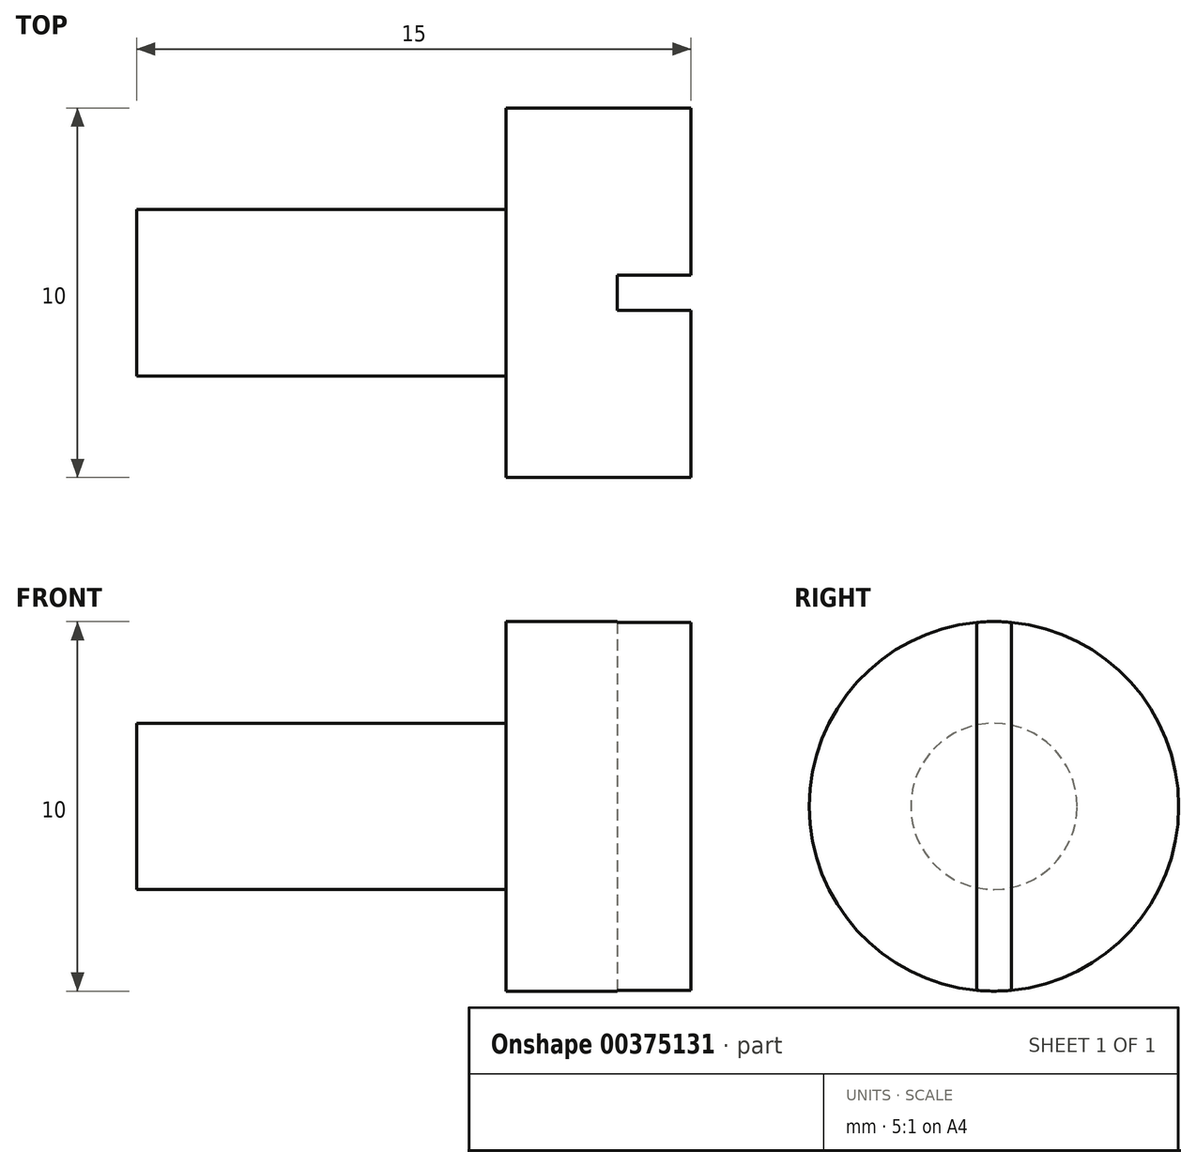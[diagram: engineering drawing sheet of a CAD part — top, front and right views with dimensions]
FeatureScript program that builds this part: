
annotation { "Feature Type Name" : "Feature", "Feature Type Description" : "" }
export const myFeature = defineFeature(function(context is Context, id is Id, definition is map)
    precondition{}
    {
        {
            var Q0;
            Q0=qCreatedBy(makeId("Right.planeOp"),FACE);
            var sketch = newSketch(context, id + "F0", { "sketchPlane" : qUnion([Q0])});
            skCircle(sketch, "E0", {"center": v(0, 0) * mm, "radius": 5 * mm});
            skSolve(sketch);
        }
        {
            var Q0;
            Q0 = qSketchRegion(id + "F0", true);
            extrude(context, id + "F1", {"entities" : qUnion([Q0]), "depth" : 5 * mm});
        }
        {
            var Q0;
            Q0=makeQuery(id+"F1.opExtrude","CAP_FACE",FACE,{"disambiguationData":[OSD([sQuery(id+"F0.wireOp",EDGE,"E0")])],"isStart":true});
            var sketch = newSketch(context, id + "F2", { "sketchPlane" : qUnion([Q0])});
            skCircle(sketch, "E1", {"center": v(0, 0) * mm, "radius": 2.25 * mm});
            skSolve(sketch);
        }
        {
            var Q0;
            Q0 = qSketchRegion(id + "F2", true);
            extrude(context, id + "F3", {"entities" : qUnion([Q0]), "operationType" : NewBodyOperationType.ADD, "depth" : 10 * mm});
        }
        {
            var Q0;
            Q0=makeQuery(id+"F1.opExtrude","CAP_FACE",FACE,{"disambiguationData":[OSD([sQuery(id+"F0.wireOp",EDGE,"E0")])],"isStart":false});
            var sketch = newSketch(context, id + "F4", { "sketchPlane" : qUnion([Q0])});
            skLineSegment(sketch, "E2.bottom", {"start": v(0.47, 6.5) * mm, "end": v(-0.47, 6.5) * mm});
            skLineSegment(sketch, "E2.top", {"start": v(0.47, -6.5) * mm, "end": v(-0.47, -6.5) * mm});
            skLineSegment(sketch, "E2.left", {"start": v(0.47, 6.5) * mm, "end": v(0.47, -6.5) * mm});
            skLineSegment(sketch, "E2.right", {"start": v(-0.47, 6.5) * mm, "end": v(-0.47, -6.5) * mm});
            skPoint(sketch, "E2.middle", {"position": v(0, 0) * mm});
            skSolve(sketch);
        }
        {
            var Q0;
            {var subQ0=sQuery(id+"F4.wireOp",EDGE,"E2.bottom");Q0=makeQuery(id+"F4.imprint","IMPRINT",FACE,{"disambiguationData":[TD([[makeQuery(id+"F4.imprint","IMPRINT",EDGE,{"derivedFrom":subQ0}),1.0]])]});}
            var Q1;
            {var subQ0=sQuery(id+"F4.wireOp",EDGE,"E2.left");var subQ1=makeQuery(id+"F1.opExtrude","CAP_EDGE",EDGE,{"disambiguationData":[OSD([sQuery(id+"F0.wireOp",EDGE,"E0")])],"isStart":false});var subQ2=makeQuery(id+"F4.imprint","INTERSECT",VERTEX,{"disambiguationData":[OD(0.0)],"derivedFrom":[subQ1,subQ0]});Q1=makeQuery(id+"F4.imprint","IMPRINT",FACE,{"disambiguationData":[TD([[makeQuery(id+"F4.imprint","IMPRINT",EDGE,{"disambiguationData":[TD([[subQ2,-1.0]])],"derivedFrom":subQ0}),-1.0]])]});}
            var Q2;
            {var subQ0=sQuery(id+"F4.wireOp",EDGE,"E2.top");Q2=makeQuery(id+"F4.imprint","IMPRINT",FACE,{"disambiguationData":[TD([[makeQuery(id+"F4.imprint","IMPRINT",EDGE,{"derivedFrom":subQ0}),-1.0]])]});}
            extrude(context, id + "F5", {"entities" : qUnion([Q0, Q1, Q2]), "operationType" : NewBodyOperationType.REMOVE, "oppositeDirection" : true, "depth" : 2 * mm});
        }
    });
